# Revit family: 2017_Fontaneria_FV-SA_2A-Triades-0106-L2_Juego-para-Bañera-y-Ducha
name_source: partatom
category: Plumbing Fixtures
revit_build: Autodesk Revit 2017 (Build: 20171027_0315(x64)
units: mm (PartAtom-declared; Revit-internal decimal feet)

## family parameters
Always vertical = Yes
Cut with Voids When Loaded = No
Host = Wall
OmniClass Number = 23.45.05.14.17
OmniClass Title = Showers
Part Type = Normal
Room Calculation Point = No
Round Connector Dimension = Use Diameter
Shared = No

## types (1)
- 106/L2 Epuyén
    AcidificacionAtmosferica = 0
    AcidificacionAtmosfericaPorUnidad = 0
    AguaConsumida = 0
    AguaConsumidaPorUnidad = 0
    Altura Cabezal = 1050 mm
    Altura Descarga = 187 mm  [stored 0.613517 ft]
    Altura Mando = 1000 mm  [stored 3.28084 ft]
    Autor = Bimetica Parametric Design Services S.L.
    Bimetica = www.bimetica.com
    CambioClimatico = 0
    CambioClimaticoPorUnidad = 0
    CosteEnergeticoKwh = 0
    CosteEnergeticoMj = 0 J
    CosteMantenimiento = 0
    Description = Juego monocomando para bañera y ducha
    Desface = 0 mm  [stored 0 ft]
    DestruccionCapaOzonoEstratosferica = 0
    DestruccionCapaOzonoEstratosfericaPorUnidad = 0
    EmisionCO2 = 0
    EnergiaNoRenovableConsumida = 0
    EnergiaNoRenovableConsumidaPorUnidad = 0
    EnergiaPrimariaTotalConsumida = 0
    EnergiaPrimariaTotalConsumidaPorUnidad = 0
    EnergiaRenovableConsumida = 0
    EnergiaRenovableConsumidaPorUnidad = 0
    Eutrofizacion = 0
    EutrofizacionPorUnidad = 0
    FactorPotencia = 0.00%
    FaltaDeRecursos = 0
    FaltaDeRecursosPorUnidad = 0
    FechaEmisionElementoBIM = 31/08/2018
    FechaVencimientoElementoBIM = 31/08/2019
    Flujo = 0.0 L/s
    FormacionFotoquimicaOzono = 0
    FormacionFotoquimicaOzonoPorUnidad = 0
    GarantiaExtendida = Yes
    IFCClasificacion = IfcValve
    InformacionTecnica = http://www.fvsa.com
    Manufacturer = FV S.A.
    MasterformatCodigo = 22 41 23
    MasterformatTitulo = Residential Showers
    MateriaPrima = 0.00%
    Material = Acero, Cromado
    Material Ducha = Acero, Cromado - Rejilla Ducha
    Material Grifo = Acero, Cromado - Rejilla
    Model = L2 Epuyén
    OmniclassCodigo = 23-31 17 00
    OmniclassTitulo = Showers
    PesoBruto = 0.00 kg
    PesoNeto = 0.00 kg
    PorcentajeApertura = 0
    ResiduoInerte = 0
    ResiduoInertePorUnidad = 0
    ResiduoRadioactivo = 0
    ResiduoRadioactivoPorUnidad = 0
    ResiduosNoPeligrosos  = 0
    ResiduosNoPeligrososPorUnidad = 0
    ResiduosPeligrosos  = 0
    ResiduosPeligrososPorUnidad = 0
    TamanoConexionDescarga = 0 mm  [stored 0 ft]
    TelefonoContacto = 0810-555-5300
    UNSPSCCodigo = 30181800
    UNSPSCTitulo = Faucet and shower heads, jets and parts and accessories
    URL = http://www.fvsa.com
    URLProducto = http://www.fvsa.com
    Uniclass2.0Codigo = 40-30-96-81
    Uniclass2.0Titulo = Shower thermostatic water supply sets
    VersionElementoBIM = V01

note: [stored X ft] marks values corroborated as IEEE doubles in the binary element streams (Revit-internal decimal feet)
